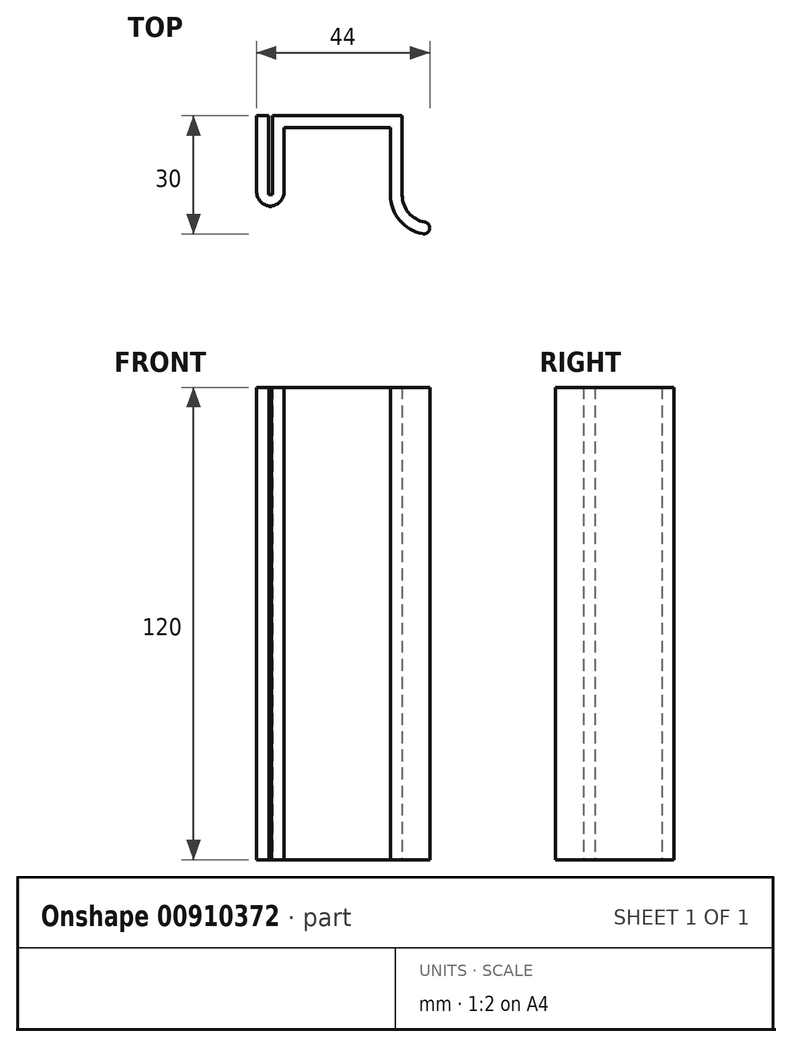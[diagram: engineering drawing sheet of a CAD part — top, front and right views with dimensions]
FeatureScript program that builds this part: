
annotation { "Feature Type Name" : "Feature", "Feature Type Description" : "" }
export const myFeature = defineFeature(function(context is Context, id is Id, definition is map)
    precondition{}
    {
        {
            var Q0;
            Q0=qCreatedBy(makeId("Top.planeOp"),FACE);
            var sketch = newSketch(context, id + "F0", { "sketchPlane" : qUnion([Q0])});
            skLineSegment(sketch, "E0", {"start": v(-1, 20) * mm, "end": v(-1, 0) * mm});
            skLineSegment(sketch, "E1", {"start": v(-1, 0) * mm, "end": v(0, 0) * mm});
            skLineSegment(sketch, "E2", {"start": v(0, 0) * mm, "end": v(0, 20) * mm});
            skLineSegment(sketch, "E3", {"start": v(0, 20) * mm, "end": v(33, 20) * mm});
            skLineSegment(sketch, "E4", {"start": v(33, 20) * mm, "end": v(33, -0.13) * mm});
            skLineSegment(sketch, "E5", {"start": v(30, -0.13) * mm, "end": v(30, 17) * mm});
            skLineSegment(sketch, "E6", {"start": v(30, 17) * mm, "end": v(3, 17) * mm});
            skLineSegment(sketch, "E7", {"start": v(3, 17) * mm, "end": v(3, 0.81) * mm});
            skLineSegment(sketch, "E8", {"start": v(-0.19, -3) * mm, "end": v(-0.81, -3) * mm});
            skLineSegment(sketch, "E9", {"start": v(-4, 0.8) * mm, "end": v(-4, 20) * mm});
            skLineSegment(sketch, "E10", {"start": v(-4, 20) * mm, "end": v(-1, 20) * mm});
            skLineSegment(sketch, "E11", {"start": v(16.5, 17) * mm, "end": v(16.5, 20) * mm, "construction": true});
            skLineSegment(sketch, "E12", {"start": v(-0.5, 0) * mm, "end": v(-0.5, -3) * mm, "construction": true});
            skLineSegment(sketch, "E13", {"start": v(3, 17) * mm, "end": v(0, 17) * mm, "construction": true});
            skLineSegment(sketch, "E14", {"start": v(30, 17) * mm, "end": v(33, 17) * mm, "construction": true});
            skArc(sketch, "E15", {"start": v(30, -0.13) * mm, "mid": v(32.33, -6.55) * mm, "end": v(38.24, -9.98) * mm});
            skArc(sketch, "E16", {"start": v(33, -0.13) * mm, "mid": v(34.63, -4.63) * mm, "end": v(38.76, -7.02) * mm});
            skArc(sketch, "E17", {"start": v(38.76, -7.02) * mm, "mid": v(39.98, -8.76) * mm, "end": v(38.24, -9.98) * mm});
            skPoint(sketch, "E18.visualSharp", {"position": v(3, -3) * mm});
            skArc(sketch, "E18.filletArc", {"start": v(-0.81, -3) * mm, "mid": v(1.88, -1.88) * mm, "end": v(3, 0.81) * mm});
            skPoint(sketch, "E19.visualSharp", {"position": v(-4, -3) * mm});
            skArc(sketch, "E19.filletArc", {"start": v(-4, 0.8) * mm, "mid": v(-2.88, -1.88) * mm, "end": v(-0.19, -3) * mm});
            skSolve(sketch);
        }
        {
            var Q0;
            Q0 = qSketchRegion(id + "F0", true);
            extrude(context, id + "F1", {"entities" : qUnion([Q0]), "depth" : 120 * mm, "offsetDistance" : 25.4 * mm});
        }
    });
